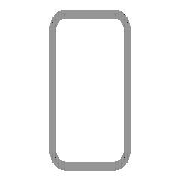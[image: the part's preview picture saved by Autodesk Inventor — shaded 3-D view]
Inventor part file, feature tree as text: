
AUTODESK INVENTOR PART (.ipt)
format: ipt  version: 2025.3 (Build 293356030, 356C)  size: 149,504 bytes
history: native  units: mm (DEFAULTED — no unit token found)
features: other x4, plane x3, split x2, sketch x1
ambient origin geometry x8: Origin, YZ Plane, XZ Plane, XY Plane, X Axis, Y Axis, Z Axis, Center Point
bodies: Solid1 (feature_tree), Body (feature_tree)
feature tree (10):
  parser-record x1  (decoder bookkeeping rows leaked as tree rows — omitted from the tree; the rows remain in map.json)
  other  "Driven Length"
  other  "Start Plane"
  other  "End Plane"
  plane  "Work Plane4"
  split  "Split1"
  plane  "Work Plane5"
  split  "Split2"
  sketch  "Sketch3"  dims[d3=2701.920698mm d4=0.0mm d7=4.0mm d9=20.0mm d11=40.0mm d12=2.0mm d13=126.334848mm d14=2828.255546mm d15=10.0mm d16=20.0mm d17=90.0deg d18=2701.920698mm]
  plane  "Work Plane3"
